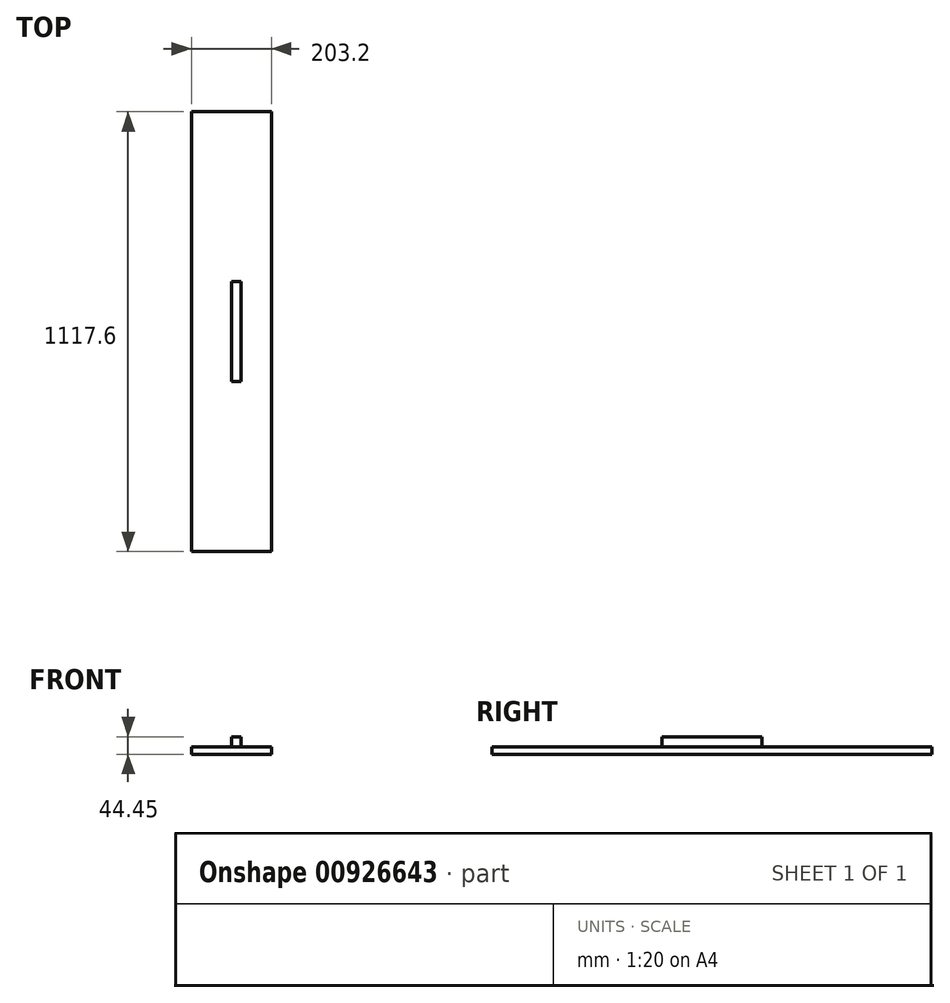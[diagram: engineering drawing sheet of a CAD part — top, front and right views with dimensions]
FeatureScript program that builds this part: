
annotation { "Feature Type Name" : "Feature", "Feature Type Description" : "" }
export const myFeature = defineFeature(function(context is Context, id is Id, definition is map)
    precondition{}
    {
        {
            var Q0;
            Q0=qCreatedBy(makeId("Front.planeOp"),FACE);
            var sketch = newSketch(context, id + "F0", { "sketchPlane" : qUnion([Q0])});
            skLineSegment(sketch, "E0.bottom", {"start": v(-101.6, 0) * mm, "end": v(101.6, 0) * mm});
            skLineSegment(sketch, "E0.top", {"start": v(-101.6, 19.05) * mm, "end": v(101.6, 19.05) * mm});
            skLineSegment(sketch, "E0.left", {"start": v(-101.6, 0) * mm, "end": v(-101.6, 19.05) * mm});
            skLineSegment(sketch, "E0.right", {"start": v(101.6, 0) * mm, "end": v(101.6, 19.05) * mm});
            skSolve(sketch);
        }
        {
            var Q0;
            Q0 = qSketchRegion(id + "F0", true);
            extrude(context, id + "F1", {"entities" : qUnion([Q0]), "endBound" : BoundingType.SYMMETRIC, "depth" : 1117.6 * mm, "offsetDistance" : 25.4 * mm});
        }
        {
            var Q0;
            Q0=qCreatedBy(makeId("Right.planeOp"),FACE);
            var sketch = newSketch(context, id + "F2", { "sketchPlane" : qUnion([Q0])});
            skLineSegment(sketch, "E1.bottom", {"start": v(-127, 19.05) * mm, "end": v(127, 19.05) * mm});
            skLineSegment(sketch, "E1.top", {"start": v(-127, 44.45) * mm, "end": v(127, 44.45) * mm});
            skLineSegment(sketch, "E1.left", {"start": v(-127, 19.05) * mm, "end": v(-127, 44.45) * mm});
            skLineSegment(sketch, "E1.right", {"start": v(127, 19.05) * mm, "end": v(127, 44.45) * mm});
            skPoint(sketch, "E2", {"position": v(0, 19.05) * mm});
            skSolve(sketch);
        }
        {
            var Q0;
            Q0 = qSketchRegion(id + "F2", true);
            extrude(context, id + "F3", {"entities" : qUnion([Q0]), "depth" : 25.4 * mm, "offsetDistance" : 25.4 * mm});
        }
    });
